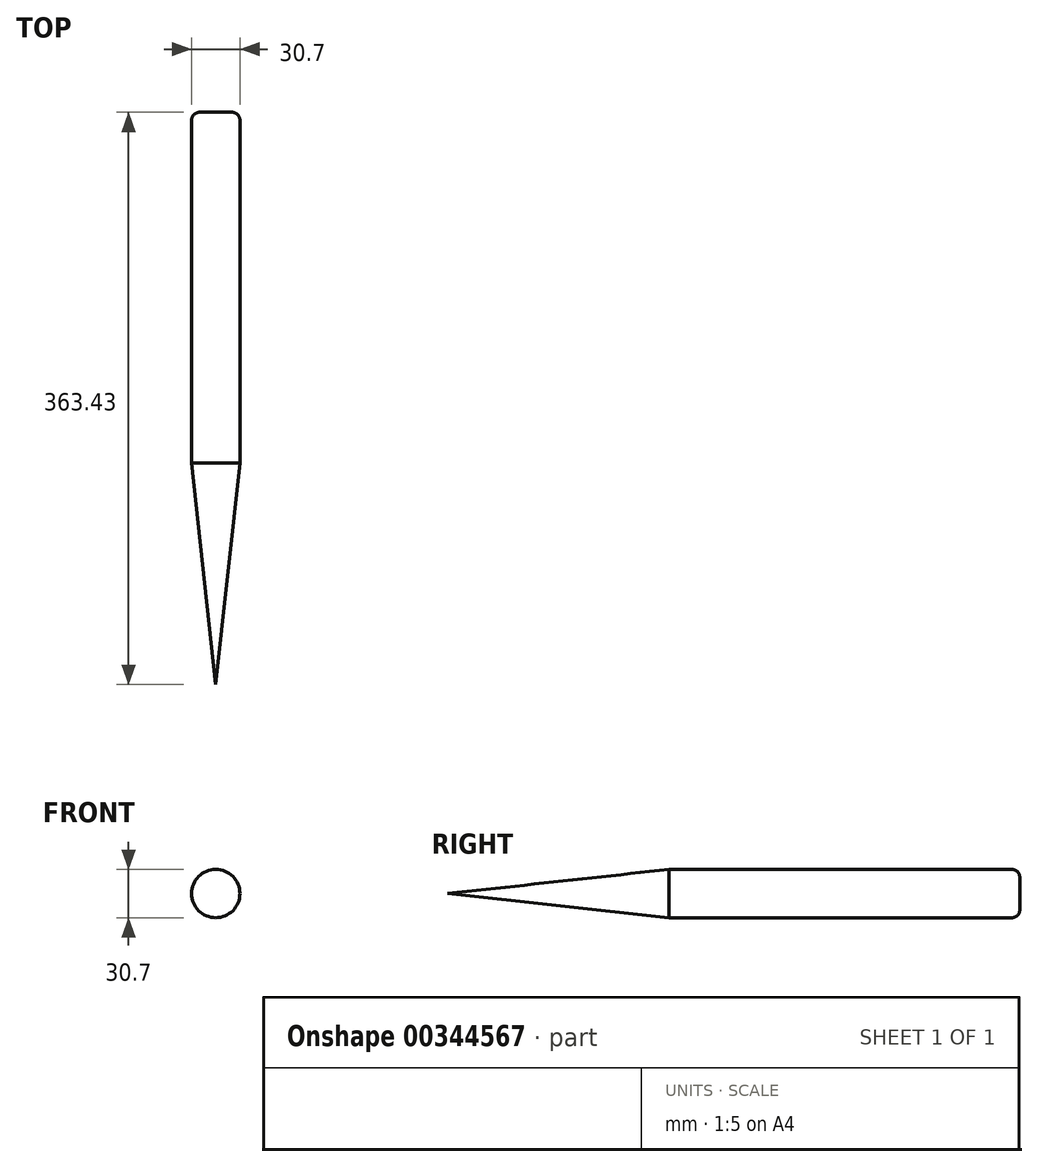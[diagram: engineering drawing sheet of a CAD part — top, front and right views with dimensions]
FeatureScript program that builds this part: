
annotation { "Feature Type Name" : "Feature", "Feature Type Description" : "" }
export const myFeature = defineFeature(function(context is Context, id is Id, definition is map)
    precondition{}
    {
        {
            var Q0;
            Q0=qCreatedBy(makeId("Front.planeOp"),FACE);
            var sketch = newSketch(context, id + "F0", { "sketchPlane" : qUnion([Q0])});
            skCircle(sketch, "E0", {"center": v(0, 0) * mm, "radius": 15.35 * mm});
            skSolve(sketch);
        }
        {
            var Q0;
            Q0=qCreatedBy(makeId("Top.planeOp"),FACE);
            var sketch = newSketch(context, id + "F1", { "sketchPlane" : qUnion([Q0])});
            skLineSegment(sketch, "E1", {"start": v(0, 109.43) * mm, "end": v(0, -113.44) * mm});
            skSolve(sketch);
        }
        {
            var Q0;
            Q0=makeQuery(id+"F0.imprint","IMPRINT",FACE,{"disambiguationData":[TD([[makeQuery(id+"F0.imprint","IMPRINT",EDGE,{"derivedFrom":sQuery(id+"F0.wireOp",EDGE,"E0")}),1.0]])]});
            var Q1;
            Q1=sQuery(id+"F1.wireOp",EDGE,"E1");
            sweep(context, id + "F2", {"profiles" : qUnion([Q0]), "path" : qUnion([Q1])});
        }
        {
            var Q0;
            Q0=qCreatedBy(makeId("Front.planeOp"),FACE);
            cPlane(context, id + "F3", {"entities" : qUnion([Q0]), "cplaneType" : CPlaneType.OFFSET, "offset" : 254 * mm, "width" : 152.4 * mm, "height" : 152.4 * mm});
        }
        {
            var Q0;
            Q0=qCreatedBy(id+"F3.planeOp",FACE);
            var sketch = newSketch(context, id + "F4", { "sketchPlane" : qUnion([Q0])});
            skCircle(sketch, "E2", {"center": v(0, 0) * mm, "radius": 3.17 * mm});
            skSolve(sketch);
        }
        {
            var Q1;
            Q1=makeQuery(id+"F2.opSweep","CAP_FACE",FACE,{"disambiguationData":[OSD([sQuery(id+"F0.wireOp",EDGE,"E0"),sQuery(id+"F1.wireOp",VERTEX,"E1.end")])],"isStart":false});
            var Q2;
            Q2=sQuery(id+"F4.wireOp",VERTEX,"E2.center");
            loft(context, id + "F5", {"operationType" : NewBodyOperationType.ADD, "sheetProfilesArray" : [{ "sheetProfileEntities" : qUnion([Q1]) }, { "sheetProfileEntities" : qUnion([Q2]) }]});
        }
        {
            var Q0;
            Q0=makeQuery(id+"F2.opSweep","CAP_EDGE",EDGE,{"disambiguationData":[OSD([sQuery(id+"F0.wireOp",EDGE,"E0"),sQuery(id+"F1.wireOp",VERTEX,"E1.start")])],"isStart":true});
            fillet(context, id + "F6", {"entities" : qUnion([Q0]), "radius" : 5.08 * mm, "tangentPropagation" : true, "allowEdgeOverflow" : false});
        }
    });
